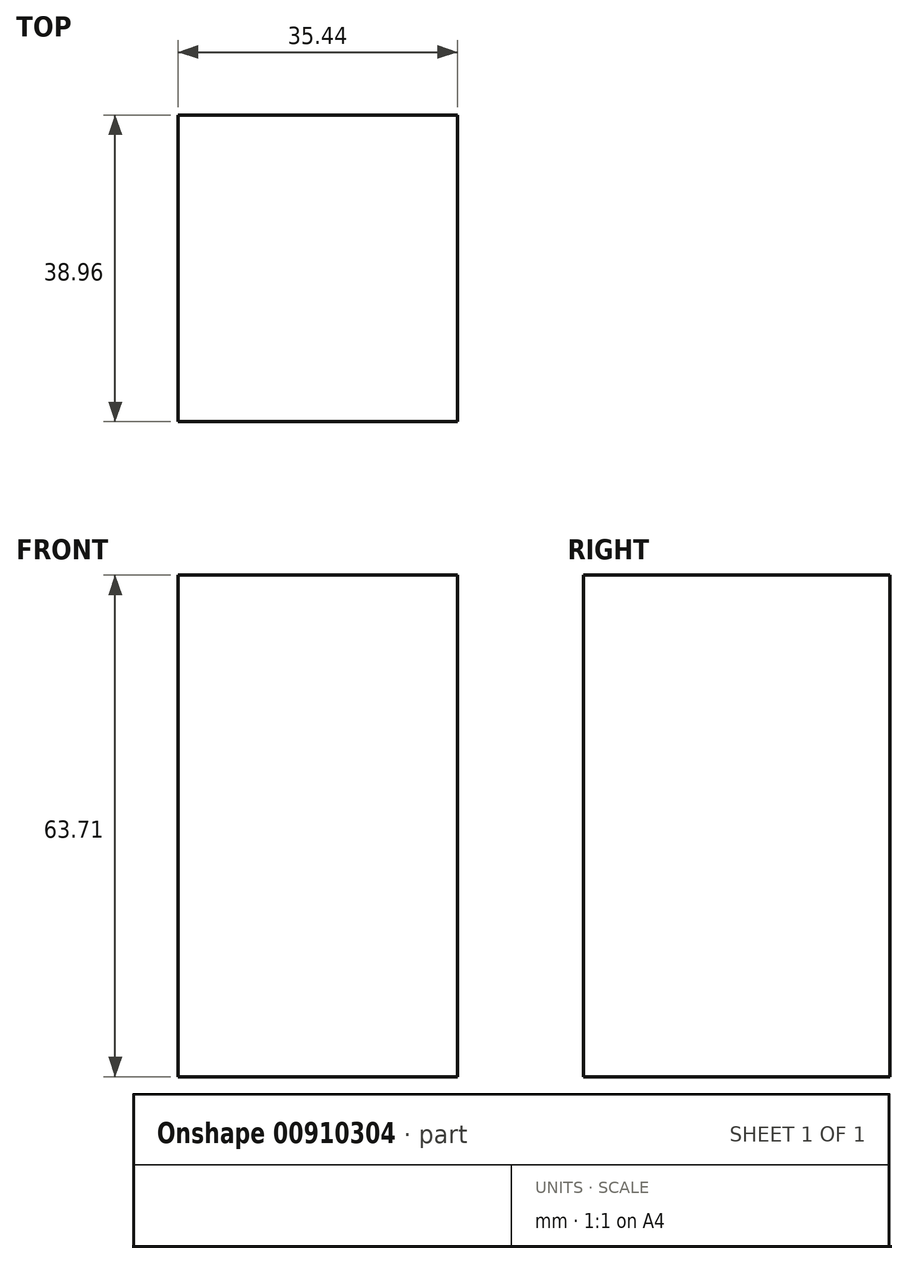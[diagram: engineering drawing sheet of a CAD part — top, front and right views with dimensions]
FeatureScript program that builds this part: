
annotation { "Feature Type Name" : "Feature", "Feature Type Description" : "" }
export const myFeature = defineFeature(function(context is Context, id is Id, definition is map)
    precondition{}
    {
        {
            var Q0;
            Q0=qCreatedBy(makeId("Top.planeOp"),FACE);
            var sketch = newSketch(context, id + "F0", { "sketchPlane" : qUnion([Q0])});
            skLineSegment(sketch, "E0.bottom", {"start": v(0, 0) * mm, "end": v(35.44, 0) * mm});
            skLineSegment(sketch, "E0.top", {"start": v(0, -38.96) * mm, "end": v(35.44, -38.96) * mm});
            skLineSegment(sketch, "E0.left", {"start": v(0, 0) * mm, "end": v(0, -38.96) * mm});
            skLineSegment(sketch, "E0.right", {"start": v(35.44, 0) * mm, "end": v(35.44, -38.96) * mm});
            skSolve(sketch);
        }
        {
            var Q0;
            Q0 = qSketchRegion(id + "F0", true);
            extrude(context, id + "F1", {"entities" : qUnion([Q0]), "depth" : 63.7 * mm, "offsetDistance" : 25.4 * mm});
        }
    });
